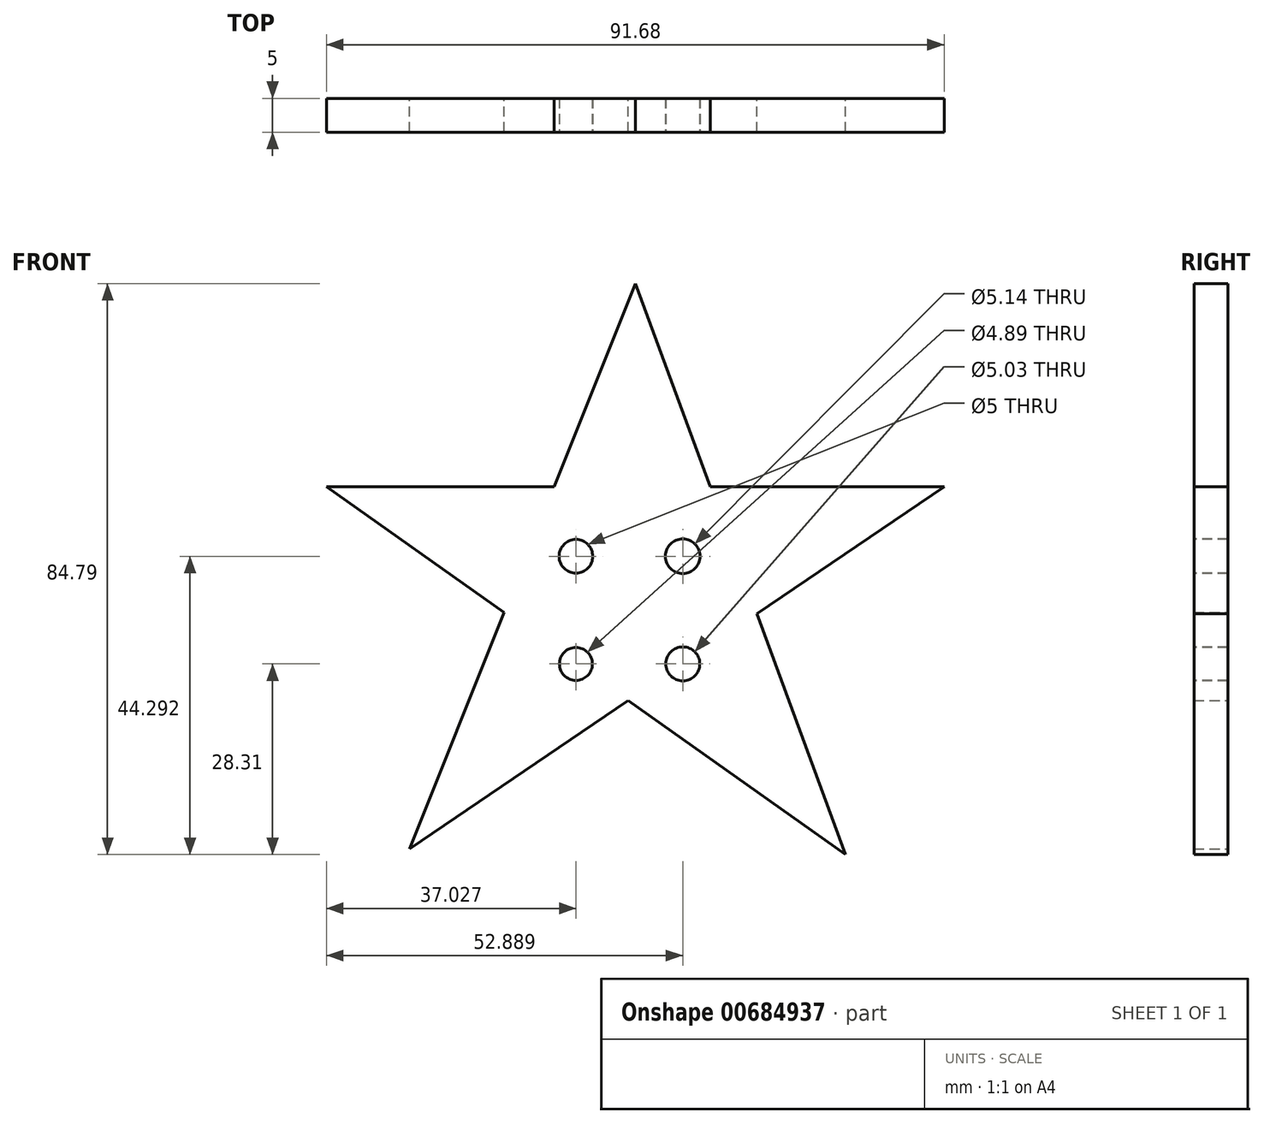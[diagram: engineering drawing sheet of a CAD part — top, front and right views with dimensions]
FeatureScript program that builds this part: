
annotation { "Feature Type Name" : "Feature", "Feature Type Description" : "" }
export const myFeature = defineFeature(function(context is Context, id is Id, definition is map)
    precondition{}
    {
        {
            var Q0;
            Q0=qCreatedBy(makeId("Front.planeOp"),FACE);
            var sketch = newSketch(context, id + "F0", { "sketchPlane" : qUnion([Q0])});
            skLineSegment(sketch, "E0", {"start": v(-33.48, -27.45) * mm, "end": v(0, 56.48) * mm});
            skLineSegment(sketch, "E1", {"start": v(0, 56.48) * mm, "end": v(31.18, -28.3) * mm});
            skLineSegment(sketch, "E2", {"start": v(31.18, -28.3) * mm, "end": v(-45.84, 26.3) * mm});
            skLineSegment(sketch, "E3", {"start": v(-45.84, 26.3) * mm, "end": v(45.84, 26.3) * mm});
            skLineSegment(sketch, "E4", {"start": v(45.84, 26.3) * mm, "end": v(-33.48, -27.45) * mm});
            skSolve(sketch);
        }
        {
            var Q0;
            {var subQ1=sQuery(id+"F0.wireOp",EDGE,"E0");var subQ5=sQuery(id+"F0.wireOp",EDGE,"E2");var subQ6=makeQuery(id+"F0.imprint","INTERSECT",VERTEX,{"derivedFrom":[subQ1,subQ5]});Q0=makeQuery(id+"F0.imprint","IMPRINT",FACE,{"disambiguationData":[TD([[makeQuery(id+"F0.imprint","IMPRINT",EDGE,{"disambiguationData":[TD([[subQ6,-1.0]])],"derivedFrom":subQ1}),-1.0]])]});}
            var Q1;
            {var subQ0=sQuery(id+"F0.wireOp",EDGE,"E1");var subQ1=sQuery(id+"F0.wireOp",EDGE,"E0");var subQ2=makeQuery(id+"F0.imprint","INTERSECT",VERTEX,{"derivedFrom":[subQ1,subQ0]});Q1=makeQuery(id+"F0.imprint","IMPRINT",FACE,{"disambiguationData":[TD([[makeQuery(id+"F0.imprint","IMPRINT",EDGE,{"disambiguationData":[TD([[subQ2,1.0]])],"derivedFrom":subQ1}),-1.0]])]});}
            var Q2;
            {var subQ0=sQuery(id+"F0.wireOp",EDGE,"E2");var subQ1=sQuery(id+"F0.wireOp",EDGE,"E0");var subQ2=makeQuery(id+"F0.imprint","INTERSECT",VERTEX,{"derivedFrom":[subQ1,subQ0]});Q2=makeQuery(id+"F0.imprint","IMPRINT",FACE,{"disambiguationData":[TD([[makeQuery(id+"F0.imprint","IMPRINT",EDGE,{"disambiguationData":[TD([[subQ2,-1.0]])],"derivedFrom":subQ1}),1.0]])]});}
            var Q3;
            {var subQ0=sQuery(id+"F0.wireOp",EDGE,"E4");var subQ1=sQuery(id+"F0.wireOp",EDGE,"E0");var subQ2=makeQuery(id+"F0.imprint","INTERSECT",VERTEX,{"derivedFrom":[subQ1,subQ0]});Q3=makeQuery(id+"F0.imprint","IMPRINT",FACE,{"disambiguationData":[TD([[makeQuery(id+"F0.imprint","IMPRINT",EDGE,{"disambiguationData":[TD([[subQ2,-1.0]])],"derivedFrom":subQ1}),-1.0]])]});}
            var Q4;
            {var subQ0=sQuery(id+"F0.wireOp",EDGE,"E2");var subQ1=sQuery(id+"F0.wireOp",EDGE,"E1");var subQ2=makeQuery(id+"F0.imprint","INTERSECT",VERTEX,{"derivedFrom":[subQ1,subQ0]});Q4=makeQuery(id+"F0.imprint","IMPRINT",FACE,{"disambiguationData":[TD([[makeQuery(id+"F0.imprint","IMPRINT",EDGE,{"disambiguationData":[TD([[subQ2,1.0]])],"derivedFrom":subQ1}),-1.0]])]});}
            var Q5;
            {var subQ0=sQuery(id+"F0.wireOp",EDGE,"E3");var subQ1=sQuery(id+"F0.wireOp",EDGE,"E1");var subQ2=makeQuery(id+"F0.imprint","INTERSECT",VERTEX,{"derivedFrom":[subQ1,subQ0]});Q5=makeQuery(id+"F0.imprint","IMPRINT",FACE,{"disambiguationData":[TD([[makeQuery(id+"F0.imprint","IMPRINT",EDGE,{"disambiguationData":[TD([[subQ2,-1.0]])],"derivedFrom":subQ1}),1.0]])]});}
            extrude(context, id + "F1", {"entities" : qUnion([Q0, Q1, Q2, Q3, Q4, Q5]), "depth" : 5 * mm, "offsetDistance" : 25 * mm});
        }
        {
            var Q0;
            Q0=makeQuery(id+"F1.opExtrude","CAP_FACE",FACE,{"disambiguationData":[OSD([sQuery(id+"F0.wireOp",EDGE,"E0"),sQuery(id+"F0.wireOp",EDGE,"E1"),sQuery(id+"F0.wireOp",EDGE,"E2"),sQuery(id+"F0.wireOp",EDGE,"E3"),sQuery(id+"F0.wireOp",EDGE,"E4")])],"isStart":false});
            var sketch = newSketch(context, id + "F2", { "sketchPlane" : qUnion([Q0])});
            skCircle(sketch, "E5", {"center": v(-8.81, 15.98) * mm, "radius": 2.5 * mm});
            skCircle(sketch, "E6", {"center": v(-8.81, 0) * mm, "radius": 2.44 * mm});
            skCircle(sketch, "E7", {"center": v(7.05, 15.98) * mm, "radius": 2.57 * mm});
            skCircle(sketch, "E8", {"center": v(7.05, 0) * mm, "radius": 2.52 * mm});
            skSolve(sketch);
        }
        {
            var Q0;
            Q0=makeQuery(id+"F2.imprint","IMPRINT",FACE,{"disambiguationData":[TD([[makeQuery(id+"F2.imprint","IMPRINT",EDGE,{"derivedFrom":sQuery(id+"F2.wireOp",EDGE,"E7")}),1.0]])]});
            var Q1;
            Q1=makeQuery(id+"F2.imprint","IMPRINT",FACE,{"disambiguationData":[TD([[makeQuery(id+"F2.imprint","IMPRINT",EDGE,{"derivedFrom":sQuery(id+"F2.wireOp",EDGE,"E6")}),1.0]])]});
            var Q2;
            Q2=makeQuery(id+"F2.imprint","IMPRINT",FACE,{"disambiguationData":[TD([[makeQuery(id+"F2.imprint","IMPRINT",EDGE,{"derivedFrom":sQuery(id+"F2.wireOp",EDGE,"E8")}),1.0]])]});
            var Q3;
            Q3=makeQuery(id+"F2.imprint","IMPRINT",FACE,{"disambiguationData":[TD([[makeQuery(id+"F2.imprint","IMPRINT",EDGE,{"derivedFrom":sQuery(id+"F2.wireOp",EDGE,"E5")}),1.0]])]});
            extrude(context, id + "F3", {"entities" : qUnion([Q0, Q1, Q2, Q3]), "operationType" : NewBodyOperationType.REMOVE, "oppositeDirection" : true, "depth" : 50 * mm, "offsetDistance" : 25 * mm});
        }
    });
